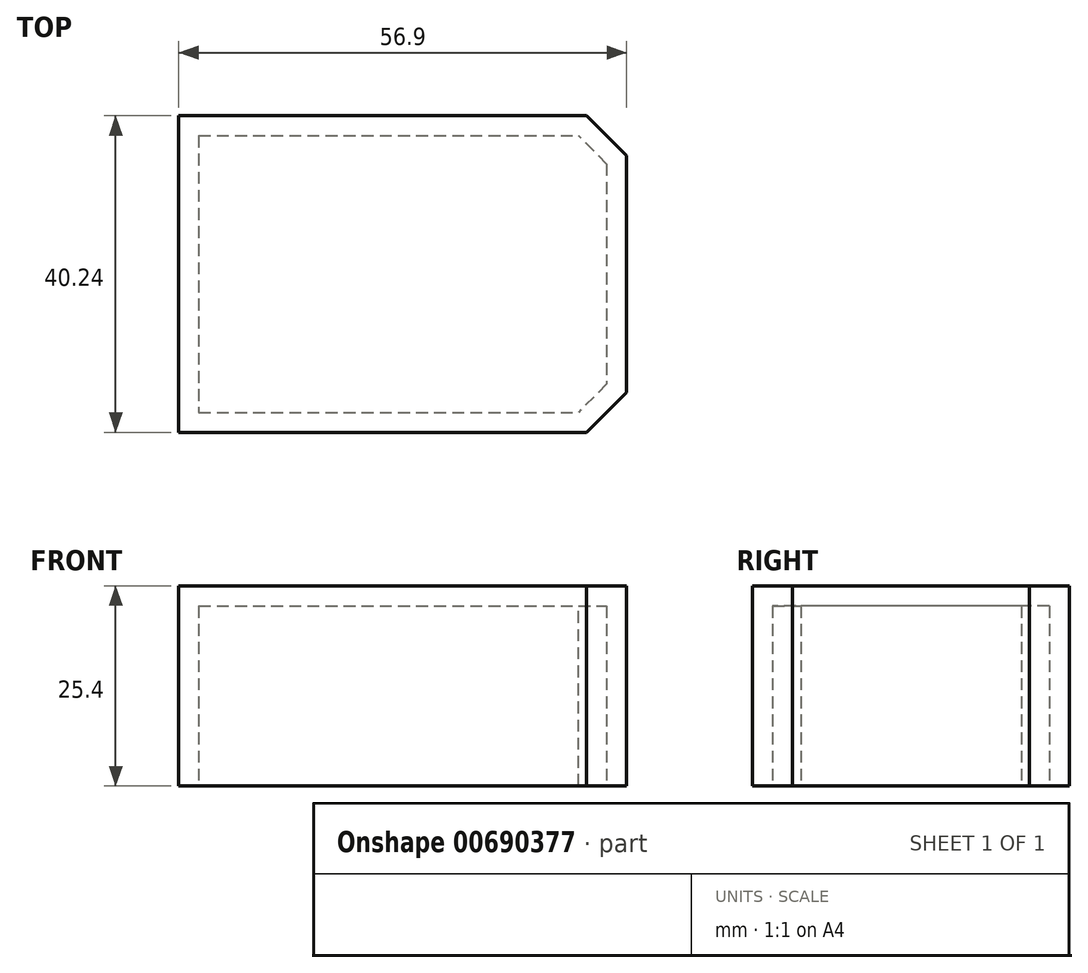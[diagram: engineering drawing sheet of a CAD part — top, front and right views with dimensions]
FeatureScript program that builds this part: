
annotation { "Feature Type Name" : "Feature", "Feature Type Description" : "" }
export const myFeature = defineFeature(function(context is Context, id is Id, definition is map)
    precondition{}
    {
        {
            var Q0;
            Q0=qCreatedBy(makeId("Top.planeOp"),FACE);
            var sketch = newSketch(context, id + "F0", { "sketchPlane" : qUnion([Q0])});
            skLineSegment(sketch, "E0.bottom", {"start": v(-16, 0) * mm, "end": v(40.9, 0) * mm});
            skLineSegment(sketch, "E0.top", {"start": v(-16, -40.24) * mm, "end": v(40.9, -40.24) * mm});
            skLineSegment(sketch, "E0.left", {"start": v(-16, 0) * mm, "end": v(-16, -40.24) * mm});
            skLineSegment(sketch, "E0.right", {"start": v(40.9, 0) * mm, "end": v(40.9, -40.24) * mm});
            skSolve(sketch);
        }
        {
            var Q0;
            Q0=makeQuery(id+"F0.imprint","IMPRINT",FACE,{"disambiguationData":[TD([[makeQuery(id+"F0.imprint","IMPRINT",EDGE,{"derivedFrom":sQuery(id+"F0.wireOp",EDGE,"E0.bottom")}),-1.0]])]});
            extrude(context, id + "F1", {"entities" : qUnion([Q0]), "depth" : 25.4 * mm, "offsetDistance" : 25.4 * mm});
        }
        {
            var Q0;
            Q0=makeQuery(id+"F1.opExtrude","SWEPT_EDGE",EDGE,{"disambiguationData":[OSD([sQuery(id+"F0.wireOp",EDGE,"E0.top"),sQuery(id+"F0.wireOp",EDGE,"E0.right")])]});
            var Q1;
            Q1=makeQuery(id+"F1.opExtrude","SWEPT_EDGE",EDGE,{"disambiguationData":[OSD([sQuery(id+"F0.wireOp",EDGE,"E0.bottom"),sQuery(id+"F0.wireOp",EDGE,"E0.right")])]});
            chamfer(context, id + "F2", {"entities" : qUnion([Q0, Q1]), "width" : 5.08 * mm, "tangentPropagation" : true});
        }
        {
            var Q0;
            Q0=qCreatedBy(makeId("Top.planeOp"),FACE);
            var sketch = newSketch(context, id + "F3", { "sketchPlane" : qUnion([Q0])});
            skCircle(sketch, "E1", {"center": v(0, -22.83) * mm, "radius": 8.75 * mm});
            skSolve(sketch);
        }
        {
            var Q0;
            Q0=sQuery(id+"F3.wireOp",EDGE,"E1");
            extrude(context, id + "F4", {"bodyType" : ToolBodyType.SURFACE, "surfaceEntities" : qUnion([Q0]), "oppositeDirection" : true, "depth" : 69.87 * mm, "offsetDistance" : 25.4 * mm});
        }
        {
            var Q0;
            Q0=makeQuery(id+"F1.opExtrude","CAP_FACE",FACE,{"disambiguationData":[OSD([sQuery(id+"F0.wireOp",EDGE,"E0.bottom"),sQuery(id+"F0.wireOp",EDGE,"E0.top"),sQuery(id+"F0.wireOp",EDGE,"E0.left"),sQuery(id+"F0.wireOp",EDGE,"E0.right")])],"isStart":true});
            shell(context, id + "F5", {"entities" : qUnion([Q0]), "thickness" : 2.54 * mm});
        }
    });
